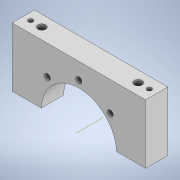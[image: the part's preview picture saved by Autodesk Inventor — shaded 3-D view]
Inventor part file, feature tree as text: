
AUTODESK INVENTOR PART (.ipt)
format: ipt  version: 2020 (Build 240168000, 168)  size: 156,672 bytes
history: native  units: in
note: dims shown in document units (in); Inventor stores cm internally (conversion verified against a paired STEP export)
features: extrude x5, sketch x4, other x1
ambient origin geometry x8: Origin, YZ Plane, XZ Plane, XY Plane, X Axis, Y Axis, Z Axis, Center Point
bodies: Solid1 (feature_tree)
feature tree (10):
  extrude  "Extrusion1"  Depth=2.0in
  extrude  "Extrusion2"  Depth=0.75in
  other  "Work Axis1"
  extrude  "Extrusion4"  TaperAngle=0.0deg  [1 undecoded]
  extrude  "Extrusion5"  Depth=2.0in
  extrude  "Extrusion6"  TaperAngle=0.0deg  [1 undecoded]
  sketch  "Sketch1"  dims[d0=4.5in d1=2.0in]
  sketch  "Sketch2"  dims[d2=0.75in d3=0.0in d4=2.54in]
  sketch  "Sketch4"  dims[d6=0.05in d7=0.0in d8=0.0in]
  sketch  "Sketch5"  dims[d27=0.2656in d28=0.375in d31=0.0in d32=0.0in d33=0.375in d34=0.159in d37=0.75in d38=0.0in d39=1.5in d40=0.2031in d42=1.1811in d44=90.0deg d46=0.0in d47=0.0in d48=2.25in d49=1.625in d50=1.625in d51=2.0in d52=2.0in d53=45.0deg]
note: 2 required parameter values undecoded (feature->parameter linkage not recoverable at this tier; creation-order binding heuristic only, values carry confidence <= 0.55)
